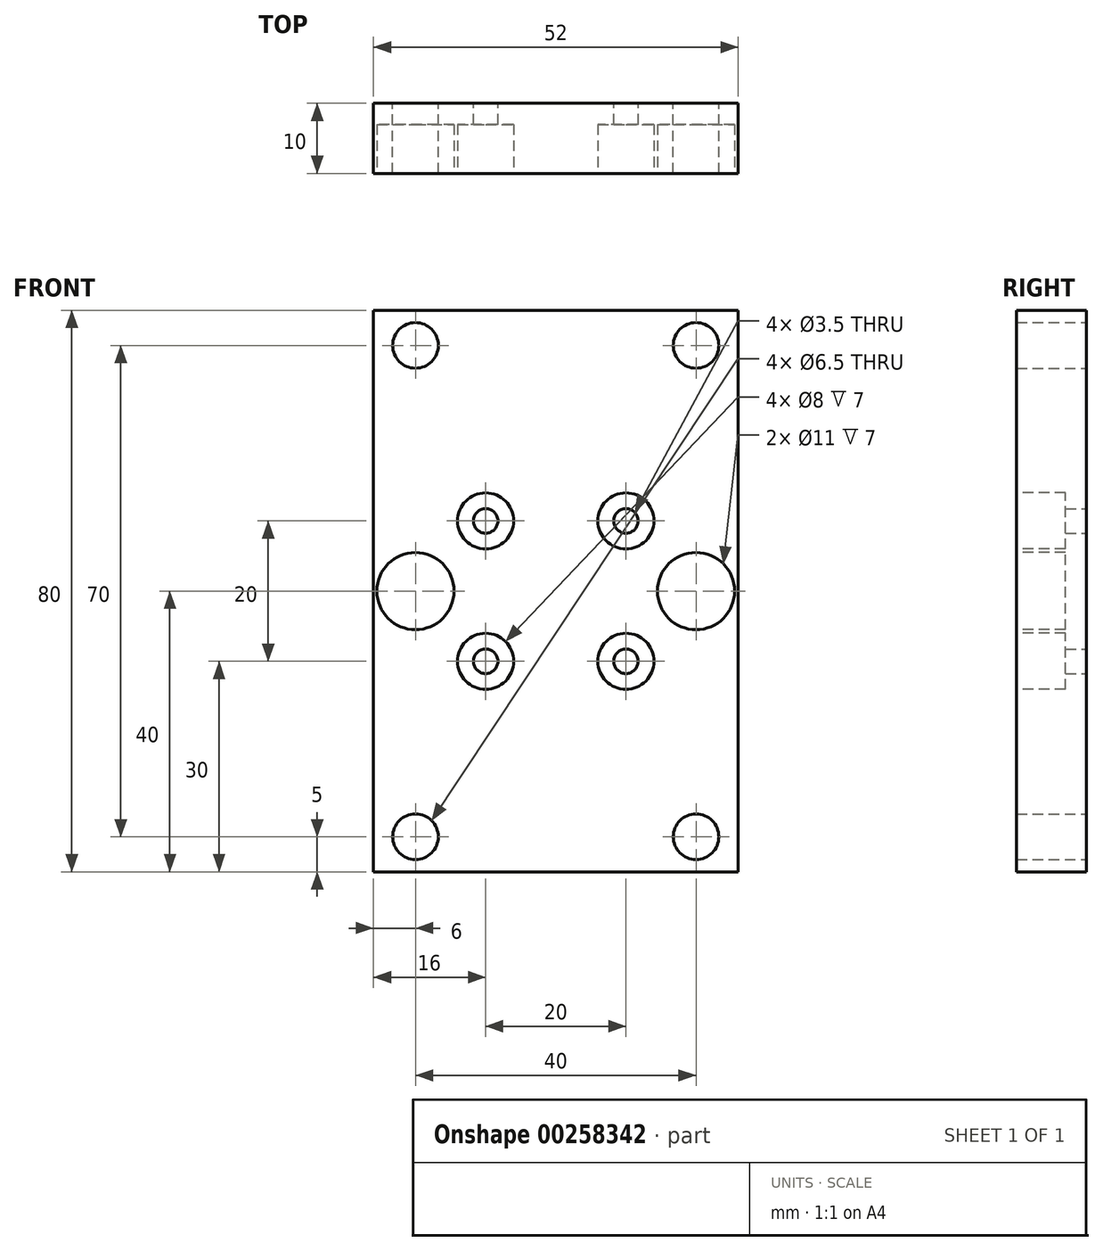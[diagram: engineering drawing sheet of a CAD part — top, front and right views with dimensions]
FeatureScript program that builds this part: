
annotation { "Feature Type Name" : "Feature", "Feature Type Description" : "" }
export const myFeature = defineFeature(function(context is Context, id is Id, definition is map)
    precondition{}
    {
        {
            var Q0;
            Q0=qCreatedBy(makeId("Front.planeOp"),FACE);
            var sketch = newSketch(context, id + "F0", { "sketchPlane" : qUnion([Q0])});
            skLineSegment(sketch, "E0.bottom", {"start": v(26, -40) * mm, "end": v(-26, -40) * mm});
            skLineSegment(sketch, "E0.top", {"start": v(26, 40) * mm, "end": v(-26, 40) * mm});
            skLineSegment(sketch, "E0.left", {"start": v(26, -40) * mm, "end": v(26, 40) * mm});
            skLineSegment(sketch, "E0.right", {"start": v(-26, -40) * mm, "end": v(-26, 40) * mm});
            skPoint(sketch, "E0.middle", {"position": v(0, 0) * mm});
            skLineSegment(sketch, "E1", {"start": v(0, 40) * mm, "end": v(0, -40) * mm, "construction": true});
            skLineSegment(sketch, "E2", {"start": v(-26, 0) * mm, "end": v(26, 0) * mm, "construction": true});
            skCircle(sketch, "E3", {"center": v(-20, 35) * mm, "radius": 3.25 * mm});
            skCircle(sketch, "E4.MirrorC", {"center": v(20, 35) * mm, "radius": 3.25 * mm});
            skCircle(sketch, "E5.MirrorC", {"center": v(-20, -35) * mm, "radius": 3.25 * mm});
            skCircle(sketch, "E6.MirrorC", {"center": v(20, -35) * mm, "radius": 3.25 * mm});
            skCircle(sketch, "E7", {"center": v(-10, 10) * mm, "radius": 1.75 * mm});
            skCircle(sketch, "E8.MirrorC", {"center": v(10, 10) * mm, "radius": 1.75 * mm});
            skCircle(sketch, "E9.MirrorC", {"center": v(-10, -10) * mm, "radius": 1.75 * mm});
            skCircle(sketch, "E10.MirrorC", {"center": v(10, -10) * mm, "radius": 1.75 * mm});
            skSolve(sketch);
        }
        {
            var Q0;
            Q0=qSketchRegion(id+"F0",true);
            extrude(context, id + "F1", {"entities" : qUnion([Q0]), "depth" : 10 * mm});
        }
        {
            var Q0;
            Q0=makeQuery(id+"F1.opExtrude","CAP_FACE",FACE,{"disambiguationData":[OSD([sQuery(id+"F0.wireOp",EDGE,"E0.bottom"),sQuery(id+"F0.wireOp",EDGE,"E0.top"),sQuery(id+"F0.wireOp",EDGE,"E0.left"),sQuery(id+"F0.wireOp",EDGE,"E0.right"),sQuery(id+"F0.wireOp",EDGE,"E3"),sQuery(id+"F0.wireOp",EDGE,"E4.MirrorC"),sQuery(id+"F0.wireOp",EDGE,"E5.MirrorC"),sQuery(id+"F0.wireOp",EDGE,"E6.MirrorC")])],"isStart":false});
            var sketch = newSketch(context, id + "F2", { "sketchPlane" : qUnion([Q0])});
            skLineSegment(sketch, "E11.0", {"start": v(0, 40) * mm, "end": v(0, -40) * mm, "construction": true});
            skLineSegment(sketch, "E11.1", {"start": v(-26, 0) * mm, "end": v(26, 0) * mm, "construction": true});
            skCircle(sketch, "E12", {"center": v(-20, 0) * mm, "radius": 5.5 * mm});
            skCircle(sketch, "E13.MirrorC", {"center": v(20, 0) * mm, "radius": 5.5 * mm});
            skSolve(sketch);
        }
        {
            var Q0;
            Q0=qSketchRegion(id+"F2",true);
            extrude(context, id + "F3", {"entities" : qUnion([Q0]), "operationType" : NewBodyOperationType.REMOVE, "oppositeDirection" : true, "depth" : 7 * mm});
        }
        {
            var Q0;
            Q0=makeQuery(id+"F1.opExtrude","CAP_FACE",FACE,{"disambiguationData":[OSD([sQuery(id+"F0.wireOp",EDGE,"E0.bottom"),sQuery(id+"F0.wireOp",EDGE,"E0.top"),sQuery(id+"F0.wireOp",EDGE,"E0.left"),sQuery(id+"F0.wireOp",EDGE,"E0.right"),sQuery(id+"F0.wireOp",EDGE,"E3"),sQuery(id+"F0.wireOp",EDGE,"E4.MirrorC"),sQuery(id+"F0.wireOp",EDGE,"E5.MirrorC"),sQuery(id+"F0.wireOp",EDGE,"E6.MirrorC"),sQuery(id+"F0.wireOp",EDGE,"E7"),sQuery(id+"F0.wireOp",EDGE,"E8.MirrorC"),sQuery(id+"F0.wireOp",EDGE,"E9.MirrorC"),sQuery(id+"F0.wireOp",EDGE,"E10.MirrorC")])],"isStart":false});
            var sketch = newSketch(context, id + "F4", { "sketchPlane" : qUnion([Q0])});
            skCircle(sketch, "E14", {"center": v(-10, 10) * mm, "radius": 4 * mm});
            skCircle(sketch, "E15", {"center": v(10, 10) * mm, "radius": 4 * mm});
            skCircle(sketch, "E16", {"center": v(-10, -10) * mm, "radius": 4 * mm});
            skCircle(sketch, "E17", {"center": v(10, -10) * mm, "radius": 4 * mm});
            skSolve(sketch);
        }
        {
            var Q0;
            Q0=qSketchRegion(id+"F4",true);
            extrude(context, id + "F5", {"entities" : qUnion([Q0]), "operationType" : NewBodyOperationType.REMOVE, "oppositeDirection" : true, "depth" : 7 * mm});
        }
    });
